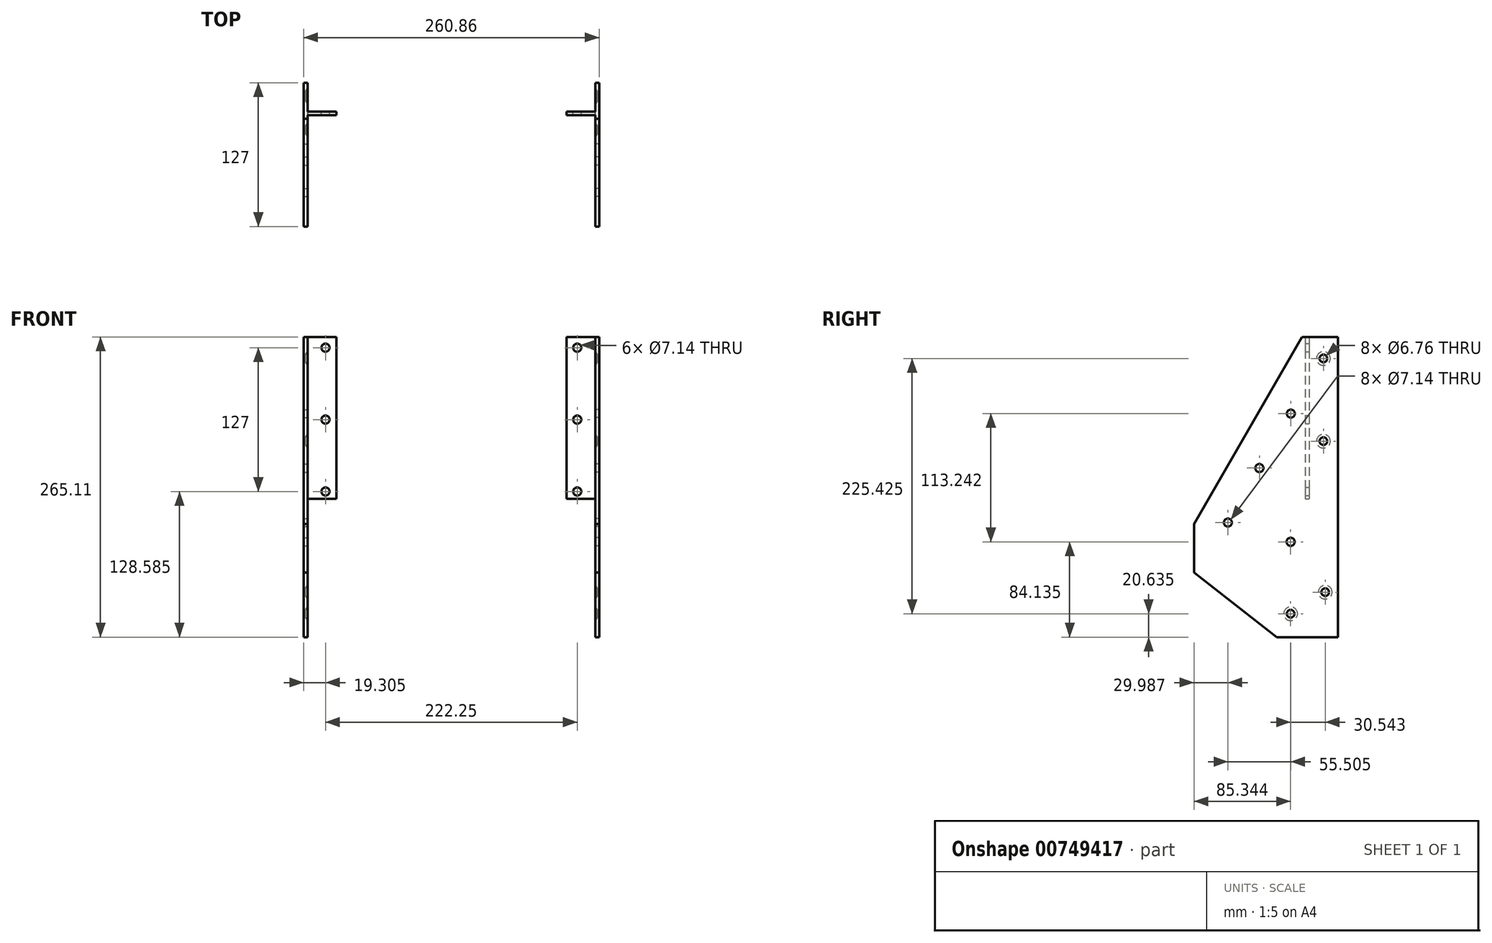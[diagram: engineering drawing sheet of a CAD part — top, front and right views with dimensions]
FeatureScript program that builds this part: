
annotation { "Feature Type Name" : "Feature", "Feature Type Description" : "" }
export const myFeature = defineFeature(function(context is Context, id is Id, definition is map)
    precondition{}
    {
        {
            var Q0;
            Q0=qCreatedBy(makeId("Right.planeOp"),FACE);
            var sketch = newSketch(context, id + "F0", { "sketchPlane" : qUnion([Q0])});
            skLineSegment(sketch, "E0.bottom", {"start": v(0, 0) * mm, "end": v(-31.75, 0) * mm});
            skLineSegment(sketch, "E0.top", {"start": v(0, -265.11) * mm, "end": v(-53.97, -265.11) * mm});
            skLineSegment(sketch, "E0.left", {"start": v(0, 0) * mm, "end": v(0, -265.11) * mm});
            skLineSegment(sketch, "E0.right", {"start": v(-127, -165.1) * mm, "end": v(-127, -207.96) * mm});
            skLineSegment(sketch, "E1", {"start": v(-31.75, 0) * mm, "end": v(-127, -165.1) * mm});
            skLineSegment(sketch, "E2", {"start": v(-127, -207.96) * mm, "end": v(-53.97, -265.11) * mm});
            skSolve(sketch);
        }
        {
            var Q0;
            Q0=makeQuery(id+"F0.imprint","IMPRINT",FACE,{"disambiguationData":[TD([[makeQuery(id+"F0.imprint","IMPRINT",EDGE,{"derivedFrom":sQuery(id+"F0.wireOp",EDGE,"E0.bottom")}),1.0]])]});
            extrude(context, id + "F1", {"entities" : qUnion([Q0]), "oppositeDirection" : true, "depth" : 3.43 * mm, "offsetDistance" : 25.4 * mm});
        }
        {
            var Q0;
            Q0=qCreatedBy(makeId("Right.planeOp"),FACE);
            var sketch = newSketch(context, id + "F2", { "sketchPlane" : qUnion([Q0])});
            skLineSegment(sketch, "E3", {"start": v(-12.7, 11.3) * mm, "end": v(-12.7, -268.25) * mm, "construction": true});
            skLineSegment(sketch, "E4", {"start": v(42.45, -19.05) * mm, "end": v(-99.2, -19.05) * mm, "construction": true});
            skLineSegment(sketch, "E5", {"start": v(48.4, -92.07) * mm, "end": v(-120.76, -92.08) * mm, "construction": true});
            skLineSegment(sketch, "E6", {"start": v(53.23, -180.98) * mm, "end": v(-109.98, -180.98) * mm, "construction": true});
            skLineSegment(sketch, "E7", {"start": v(55.13, -225.43) * mm, "end": v(-47.57, -225.43) * mm, "construction": true});
            skLineSegment(sketch, "E8", {"start": v(58.43, -244.48) * mm, "end": v(-51, -244.48) * mm, "construction": true});
            skLineSegment(sketch, "E9", {"start": v(-11.11, -211.38) * mm, "end": v(-11.11, -271.97) * mm, "construction": true});
            skLineSegment(sketch, "E10", {"start": v(-41.66, -176.36) * mm, "end": v(-41.66, -271.97) * mm, "construction": true});
            skLineSegment(sketch, "E11", {"start": v(-31.75, 0) * mm, "end": v(69.32, -58.3) * mm, "construction": true});
            skLineSegment(sketch, "E12", {"start": v(-63.48, -55) * mm, "end": v(42.67, -116.24) * mm, "construction": true});
            skLineSegment(sketch, "E13", {"start": v(-91.25, -103.13) * mm, "end": v(10.79, -162) * mm, "construction": true});
            skLineSegment(sketch, "E14", {"start": v(-119.01, -151.26) * mm, "end": v(-73.05, -177.77) * mm, "construction": true});
            skLineSegment(sketch, "E15", {"start": v(12.85, 26.48) * mm, "end": v(-135.53, -230.7) * mm, "construction": true});
            skPoint(sketch, "E16", {"position": v(-12.7, -19.05) * mm});
            skPoint(sketch, "E17", {"position": v(-12.7, -92.08) * mm});
            skPoint(sketch, "E18", {"position": v(-11.11, -225.43) * mm});
            skPoint(sketch, "E19", {"position": v(-41.66, -244.48) * mm});
            skPoint(sketch, "E20", {"position": v(-41.66, -180.98) * mm});
            skPoint(sketch, "E21", {"position": v(-97.01, -163.95) * mm});
            skPoint(sketch, "E22", {"position": v(-69.25, -115.82) * mm});
            skPoint(sketch, "E23", {"position": v(-41.48, -67.7) * mm});
            skPoint(sketch, "E24", {"position": v(-41.5, -67.73) * mm});
            skSolve(sketch);
        }
        {
            var Q0;
            Q0=sQuery(id+"F2.wireOp",VERTEX,"E16");
            var Q1;
            Q1=sQuery(id+"F2.wireOp",VERTEX,"E17");
            var Q2;
            Q2=sQuery(id+"F2.wireOp",VERTEX,"E18");
            var Q3;
            Q3=sQuery(id+"F2.wireOp",VERTEX,"E19");
            var Q4;
            Q4=makeQuery(id+"F1.opExtrude","SWEPT_BODY",BODY,{"disambiguationData":[OSD([sQuery(id+"F0.wireOp",EDGE,"E0.bottom"),sQuery(id+"F0.wireOp",EDGE,"E0.top"),sQuery(id+"F0.wireOp",EDGE,"E0.left"),sQuery(id+"F0.wireOp",EDGE,"E0.right"),sQuery(id+"F0.wireOp",EDGE,"E1"),sQuery(id+"F0.wireOp",EDGE,"E2")])]});
            hole(context, id + "F3", {"style" : HoleStyle.C_SINK, "endStyle" : HoleEndStyle.THROUGH, "holeDiameter" : 6.76 * mm, "cSinkDiameter" : 12.2 * mm, "cSinkAngle" : 110 * degree, "majorDiameter" : 6.35 * mm, "isTappedThrough" : true, "tappedDepth" : 12.7 * mm, "tapClearance" : 3, "locations" : qUnion([Q0, Q1, Q2, Q3]), "scope" : qUnion([Q4])});
        }
        {
            var Q0;
            Q0=sQuery(id+"F2.wireOp",VERTEX,"E24");
            var Q1;
            Q1=sQuery(id+"F2.wireOp",VERTEX,"E22");
            var Q2;
            Q2=sQuery(id+"F2.wireOp",VERTEX,"E21");
            var Q3;
            Q3=sQuery(id+"F2.wireOp",VERTEX,"E20");
            var Q4;
            Q4=makeQuery(id+"F1.opExtrude","SWEPT_BODY",BODY,{"disambiguationData":[OSD([sQuery(id+"F0.wireOp",EDGE,"E0.bottom"),sQuery(id+"F0.wireOp",EDGE,"E0.top"),sQuery(id+"F0.wireOp",EDGE,"E0.left"),sQuery(id+"F0.wireOp",EDGE,"E0.right"),sQuery(id+"F0.wireOp",EDGE,"E1"),sQuery(id+"F0.wireOp",EDGE,"E2")])]});
            hole(context, id + "F4", {"style" : HoleStyle.SIMPLE, "endStyle" : HoleEndStyle.THROUGH, "holeDiameter" : 7.14 * mm, "majorDiameter" : 6.35 * mm, "isTappedThrough" : true, "tappedDepth" : 12.7 * mm, "tapClearance" : 3, "locations" : qUnion([Q0, Q1, Q2, Q3]), "scope" : qUnion([Q4])});
        }
        {
            var Q0;
            Q0=qCreatedBy(makeId("Right.planeOp"),FACE);
            var sketch = newSketch(context, id + "F5", { "sketchPlane" : qUnion([Q0])});
            skLineSegment(sketch, "E25.0", {"start": v(0, 0) * mm, "end": v(0, -265.11) * mm});
            skLineSegment(sketch, "E26", {"start": v(-25.4, 0) * mm, "end": v(-25.4, -142.88) * mm});
            skLineSegment(sketch, "E27.0", {"start": v(-28.83, 0) * mm, "end": v(-28.83, -142.88) * mm});
            skLineSegment(sketch, "E28", {"start": v(-28.83, 0) * mm, "end": v(-25.4, 0) * mm});
            skLineSegment(sketch, "E29", {"start": v(-28.83, -142.88) * mm, "end": v(-25.4, -142.88) * mm});
            skLineSegment(sketch, "E30.0", {"start": v(-25.4, 0) * mm, "end": v(-28.83, 0) * mm});
            skPoint(sketch, "E31.orphan", {"position": v(-31.75, 0) * mm});
            skSolve(sketch);
        }
        {
            var Q0;
            Q0=makeQuery(id+"F5.imprint","IMPRINT",FACE,{"disambiguationData":[TD([[makeQuery(id+"F5.imprint","IMPRINT",EDGE,{"derivedFrom":sQuery(id+"F5.wireOp",EDGE,"E26")}),-1.0]])]});
            extrude(context, id + "F6", {"entities" : qUnion([Q0]), "operationType" : NewBodyOperationType.ADD, "depth" : 25.4 * mm, "offsetDistance" : 25.4 * mm});
        }
        {
            var Q0;
            Q0=makeQuery(id+"F6.opExtrude","SWEPT_FACE",FACE,{"disambiguationData":[OSD([sQuery(id+"F5.wireOp",EDGE,"E26")])]});
            var sketch = newSketch(context, id + "F7", { "sketchPlane" : qUnion([Q0])});
            skLineSegment(sketch, "E32.0", {"start": v(0, 0) * mm, "end": v(0, -265.11) * mm});
            skLineSegment(sketch, "E33", {"start": v(-15.88, 4.53) * mm, "end": v(-15.88, -151.43) * mm, "construction": true});
            skLineSegment(sketch, "E34.0", {"start": v(-25.4, 0) * mm, "end": v(0, 0) * mm});
            skLineSegment(sketch, "E35", {"start": v(-40.94, -9.52) * mm, "end": v(20.96, -9.52) * mm, "construction": true});
            skLineSegment(sketch, "E36", {"start": v(-45.21, -73.03) * mm, "end": v(24.3, -73.03) * mm, "construction": true});
            skLineSegment(sketch, "E37", {"start": v(-42.98, -136.53) * mm, "end": v(18.73, -136.53) * mm, "construction": true});
            skPoint(sketch, "E38", {"position": v(-15.88, -9.52) * mm});
            skPoint(sketch, "E39", {"position": v(-15.88, -73.03) * mm});
            skPoint(sketch, "E40", {"position": v(-15.88, -136.53) * mm});
            skSolve(sketch);
        }
        {
            var Q0;
            Q0=sQuery(id+"F7.wireOp",VERTEX,"E38");
            var Q1;
            Q1=sQuery(id+"F7.wireOp",VERTEX,"E39");
            var Q2;
            Q2=sQuery(id+"F7.wireOp",VERTEX,"E40");
            var Q3;
            Q3=makeQuery(id+"F1.opExtrude","SWEPT_BODY",BODY,{"disambiguationData":[OSD([sQuery(id+"F0.wireOp",EDGE,"E0.bottom"),sQuery(id+"F0.wireOp",EDGE,"E0.top"),sQuery(id+"F0.wireOp",EDGE,"E0.left"),sQuery(id+"F0.wireOp",EDGE,"E0.right"),sQuery(id+"F0.wireOp",EDGE,"E1"),sQuery(id+"F0.wireOp",EDGE,"E2")])]});
            hole(context, id + "F8", {"style" : HoleStyle.SIMPLE, "endStyle" : HoleEndStyle.THROUGH, "holeDiameter" : 7.14 * mm, "majorDiameter" : 6.35 * mm, "isTappedThrough" : true, "tappedDepth" : 12.7 * mm, "tapClearance" : 3, "locations" : qUnion([Q0, Q1, Q2]), "scope" : qUnion([Q3])});
        }
        {
            var Q0;
            Q0=qCreatedBy(makeId("Right.planeOp"),FACE);
            cPlane(context, id + "F9", {"entities" : qUnion([Q0]), "cplaneType" : CPlaneType.OFFSET, "offset" : 127 * mm, "width" : 152.4 * mm, "height" : 152.4 * mm});
        }
        {
            var Q0;
            Q0=makeQuery(id+"F1.opExtrude","SWEPT_BODY",BODY,{"disambiguationData":[OSD([sQuery(id+"F0.wireOp",EDGE,"E0.bottom"),sQuery(id+"F0.wireOp",EDGE,"E0.top"),sQuery(id+"F0.wireOp",EDGE,"E0.left"),sQuery(id+"F0.wireOp",EDGE,"E0.right"),sQuery(id+"F0.wireOp",EDGE,"E1"),sQuery(id+"F0.wireOp",EDGE,"E2")])]});
            var Q1;
            Q1=qCreatedBy(id+"F9.planeOp",FACE);
            mirror(context, id + "F10", {"entities" : qUnion([Q0]), "mirrorPlane" : qUnion([Q1])});
        }
    });
